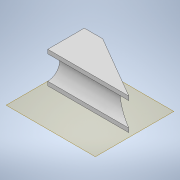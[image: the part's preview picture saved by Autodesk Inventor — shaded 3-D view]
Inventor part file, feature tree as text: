
AUTODESK INVENTOR PART (.ipt)
format: ipt  version: 2022.3 (Build 263350000, 350)  size: 120,320 bytes
history: native  units: mm
features: extrude x3, sketch x3, thicken_offset x2, other x2, plane x1, reference x1
ambient origin geometry x8: Origin, YZ Plane, XZ Plane, XY Plane, X Axis, Y Axis, Z Axis, Center Point
bodies: Solid1 (feature_tree)
feature tree (12):
  plane  "Work Plane1"
  extrude  "Extrusion1"  Depth=8.0mm
  extrude  "Extrusion2"  Depth=0.2mm
  thicken_offset  "Thicken1"
  thicken_offset  "Thicken2"
  extrude  "Extrusion3"  Depth=0.2mm
  sketch  "Sketch1"  dims[d0=8.0mm d1=0.0mm d2=6.0mm]
  reference  "Reference1"
  sketch  "Sketch2"  dims[d3=15.981mm d4=0.0mm d5=0.2mm]
  sketch  "Sketch3"  dims[d6=0.2mm d7=0.2mm d8=0.2mm d9=0.0mm d10=0.0mm]
  other  "v2.0.iam"
  other  "Base:1"
